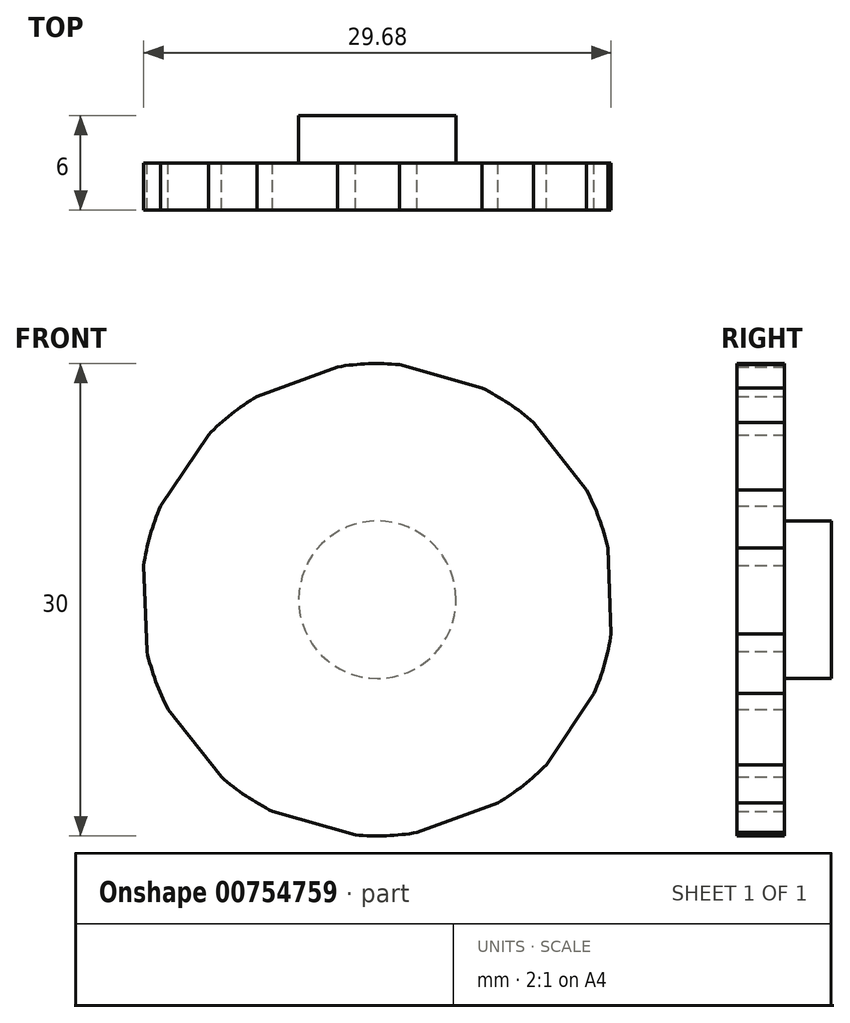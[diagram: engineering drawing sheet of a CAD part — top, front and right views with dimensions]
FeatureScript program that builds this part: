
annotation { "Feature Type Name" : "Feature", "Feature Type Description" : "" }
export const myFeature = defineFeature(function(context is Context, id is Id, definition is map)
    precondition{}
    {
        {
            var Q0;
            Q0=qCreatedBy(makeId("Front.planeOp"),FACE);
            var sketch = newSketch(context, id + "F0", { "sketchPlane" : qUnion([Q0])});
            skCircle(sketch, "E0", {"center": v(0, 0) * mm, "radius": 5 * mm});
            skSolve(sketch);
        }
        {
            var Q0;
            Q0=qSketchRegion(id+"F0",true);
            extrude(context, id + "F1", {"entities" : qUnion([Q0]), "depth" : 3 * mm, "offsetDistance" : 25 * mm});
        }
        {
            var Q0;
            Q0=makeQuery(id+"F1.opExtrude","CAP_FACE",FACE,{"disambiguationData":[OSD([sQuery(id+"F0.wireOp",EDGE,"E0")])],"isStart":false});
            var sketch = newSketch(context, id + "F2", { "sketchPlane" : qUnion([Q0])});
            skCircle(sketch, "E1", {"center": v(0, 0) * mm, "radius": 15 * mm});
            skSolve(sketch);
        }
        {
            var Q0;
            Q0=qSketchRegion(id+"F2",true);
            extrude(context, id + "F3", {"entities" : qUnion([Q0]), "operationType" : NewBodyOperationType.ADD, "depth" : 3 * mm, "offsetDistance" : 25 * mm});
        }
        {
            var Q0;
            Q0=makeQuery(id+"F3.opExtrude","CAP_FACE",FACE,{"disambiguationData":[OSD([sQuery(id+"F2.wireOp",EDGE,"E1")])],"isStart":false});
            var sketch = newSketch(context, id + "F4", { "sketchPlane" : qUnion([Q0])});
            skCircle(sketch, "E2.cCircle", {"center": v(0, 0) * mm, "radius": 14.75 * mm, "construction": true});
            skLineSegment(sketch, "E2.0", {"start": v(-0.59, 15.5) * mm, "end": v(8.63, 12.88) * mm});
            skLineSegment(sketch, "E2.1", {"start": v(8.63, 12.88) * mm, "end": v(14.56, 5.35) * mm});
            skLineSegment(sketch, "E2.2", {"start": v(14.56, 5.35) * mm, "end": v(14.92, -4.23) * mm});
            skLineSegment(sketch, "E2.3", {"start": v(14.92, -4.23) * mm, "end": v(9.59, -12.2) * mm});
            skLineSegment(sketch, "E2.4", {"start": v(9.59, -12.2) * mm, "end": v(0.59, -15.5) * mm});
            skLineSegment(sketch, "E2.5", {"start": v(0.59, -15.5) * mm, "end": v(-8.63, -12.88) * mm});
            skLineSegment(sketch, "E2.6", {"start": v(-8.63, -12.88) * mm, "end": v(-14.56, -5.35) * mm});
            skLineSegment(sketch, "E2.7", {"start": v(-14.56, -5.35) * mm, "end": v(-14.92, 4.23) * mm});
            skLineSegment(sketch, "E2.8", {"start": v(-14.92, 4.23) * mm, "end": v(-9.59, 12.2) * mm});
            skLineSegment(sketch, "E2.9", {"start": v(-9.59, 12.2) * mm, "end": v(-0.59, 15.5) * mm});
            skPoint(sketch, "E2.0.midPoint", {"position": v(4.02, 14.2) * mm});
            skCircle(sketch, "E3", {"center": v(0, 0) * mm, "radius": 17.22 * mm});
            skSolve(sketch);
        }
        {
            var Q0;
            Q0=qSketchRegion(id+"F4",true);
            extrude(context, id + "F5", {"entities" : qUnion([Q0]), "operationType" : NewBodyOperationType.REMOVE, "oppositeDirection" : true, "depth" : 25 * mm, "offsetDistance" : 25 * mm});
        }
    });
